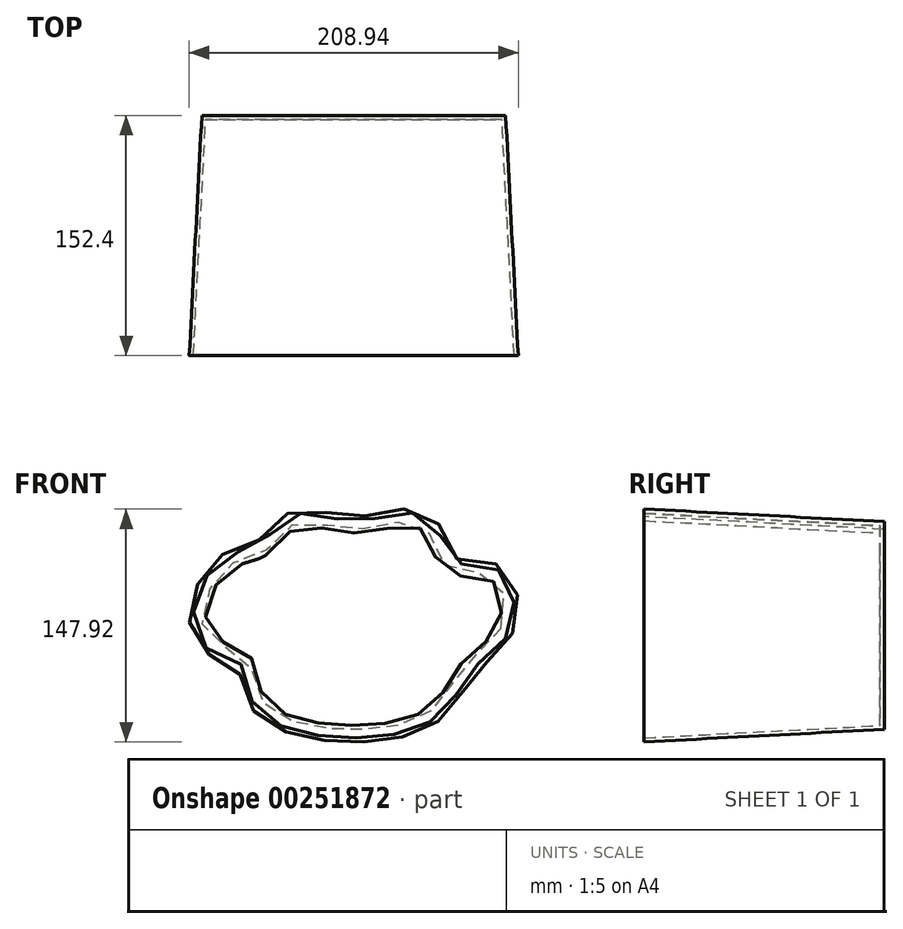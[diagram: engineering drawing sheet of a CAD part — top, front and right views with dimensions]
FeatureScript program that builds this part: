
annotation { "Feature Type Name" : "Feature", "Feature Type Description" : "" }
export const myFeature = defineFeature(function(context is Context, id is Id, definition is map)
    precondition{}
    {
        {
            var Q0;
            Q0=qCreatedBy(makeId("Front.planeOp"),FACE);
            var sketch = newSketch(context, id + "F0", { "sketchPlane" : qUnion([Q0])});
            skFitSpline(sketch, "E0", {"points": [v(-70.78, 44.88) * mm, v(-44, 57) * mm, v(-23.62, 75.02) * mm, v(13.66, 71.22) * mm, v(56.63, 73.83) * mm, v(72.78, 46.52) * mm, v(102.22, 40.59) * mm, v(106.5, 8.3) * mm, v(84.14, -14.4) * mm, v(65.33, -41.5) * mm, v(15.29, -55.85) * mm, v(-45, -38.48) * mm, v(-56.39, -8.8) * mm, v(-81.08, 3.55) * mm, v(-70.78, 44.88) * mm]});
            skSolve(sketch);
        }
        {
            var Q0;
            Q0=makeQuery(id+"F0.imprint","IMPRINT",FACE,{"disambiguationData":[TD([[makeQuery(id+"F0.imprint","IMPRINT",EDGE,{"derivedFrom":sQuery(id+"F0.wireOp",EDGE,"E0")}),-1.0]])]});
            extrude(context, id + "F1", {"entities" : qUnion([Q0]), "depth" : 152.4 * mm, "hasDraft" : true, "draftAngle" : 3 * degree});
        }
        {
            var Q0;
            Q0=makeQuery(id+"F1.opExtrude","CAP_FACE",FACE,{"disambiguationData":[OSD([sQuery(id+"F0.wireOp",EDGE,"E0")])],"isStart":false});
            shell(context, id + "F2", {"entities" : qUnion([Q0]), "thickness" : 2.54 * mm});
        }
    });
